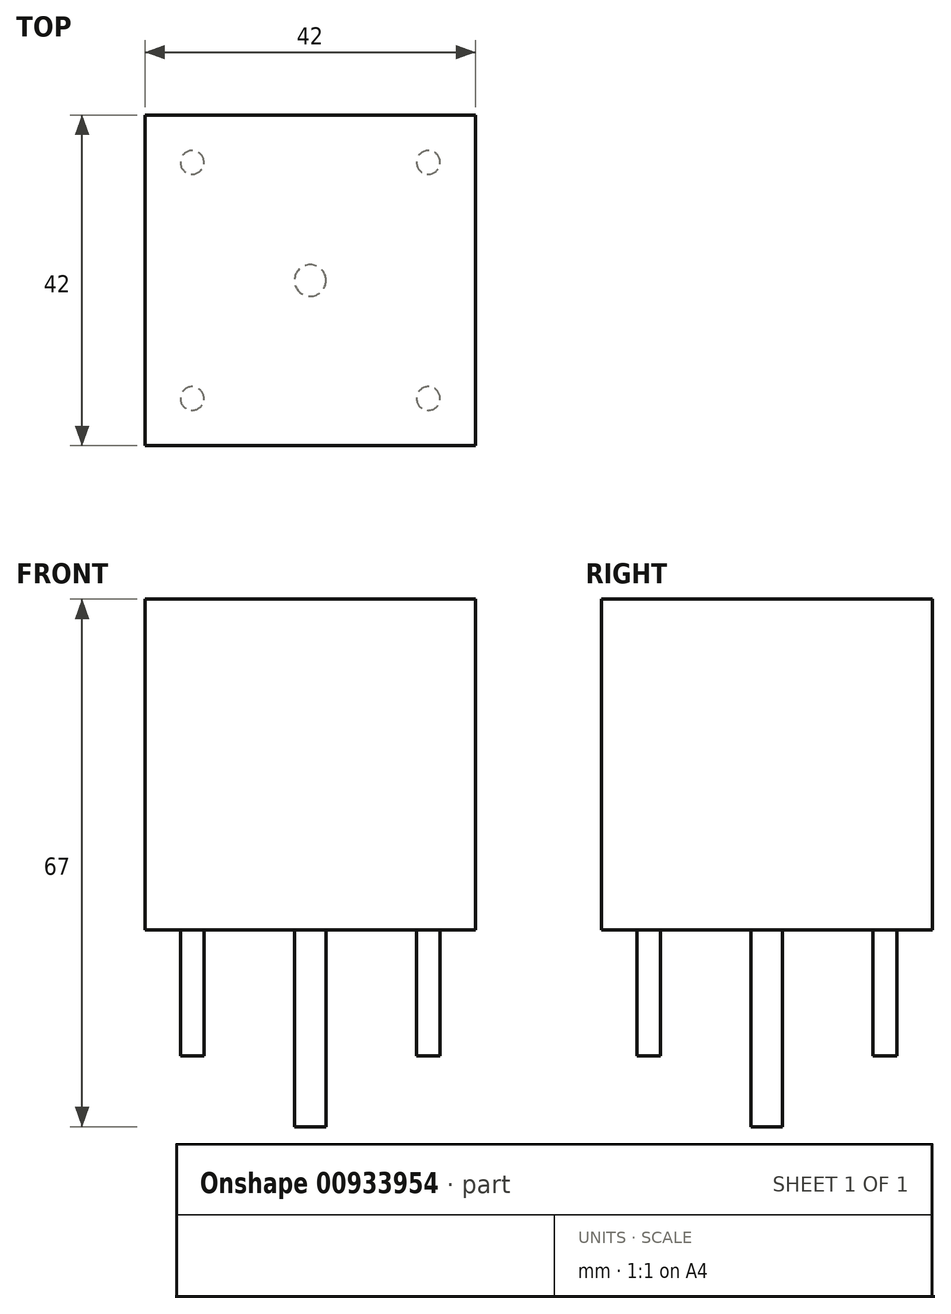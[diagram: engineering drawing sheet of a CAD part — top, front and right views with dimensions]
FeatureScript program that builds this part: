
annotation { "Feature Type Name" : "Feature", "Feature Type Description" : "" }
export const myFeature = defineFeature(function(context is Context, id is Id, definition is map)
    precondition{}
    {
        {
            var Q0;
            Q0=qCreatedBy(makeId("Top.planeOp"),FACE);
            var sketch = newSketch(context, id + "F0", { "sketchPlane" : qUnion([Q0])});
            skLineSegment(sketch, "E0.bottom", {"start": v(21, -21) * mm, "end": v(-21, -21) * mm});
            skLineSegment(sketch, "E0.top", {"start": v(21, 21) * mm, "end": v(-21, 21) * mm});
            skLineSegment(sketch, "E0.left", {"start": v(21, -21) * mm, "end": v(21, 21) * mm});
            skLineSegment(sketch, "E0.right", {"start": v(-21, -21) * mm, "end": v(-21, 21) * mm});
            skPoint(sketch, "E0.middle", {"position": v(0, 0) * mm});
            skSolve(sketch);
        }
        {
            var Q0;
            Q0=makeQuery(id+"F0.imprint","IMPRINT",FACE,{"disambiguationData":[TD([[makeQuery(id+"F0.imprint","IMPRINT",EDGE,{"derivedFrom":sQuery(id+"F0.wireOp",EDGE,"E0.bottom")}),-1.0]])]});
            extrude(context, id + "F1", {"entities" : qUnion([Q0]), "depth" : 42 * mm, "offsetDistance" : 25 * mm});
        }
        {
            var Q0;
            Q0=makeQuery(id+"F1.opExtrude","CAP_FACE",FACE,{"disambiguationData":[OSD([sQuery(id+"F0.wireOp",EDGE,"E0.bottom"),sQuery(id+"F0.wireOp",EDGE,"E0.top"),sQuery(id+"F0.wireOp",EDGE,"E0.left"),sQuery(id+"F0.wireOp",EDGE,"E0.right")])],"isStart":true});
            var sketch = newSketch(context, id + "F2", { "sketchPlane" : qUnion([Q0])});
            skCircle(sketch, "E1", {"center": v(0, 0) * mm, "radius": 2 * mm});
            skSolve(sketch);
        }
        {
            var Q0;
            Q0=makeQuery(id+"F2.imprint","IMPRINT",FACE,{"disambiguationData":[TD([[makeQuery(id+"F2.imprint","IMPRINT",EDGE,{"derivedFrom":sQuery(id+"F2.wireOp",EDGE,"E1")}),1.0]])]});
            extrude(context, id + "F3", {"entities" : qUnion([Q0]), "operationType" : NewBodyOperationType.ADD, "depth" : 25 * mm, "offsetDistance" : 25 * mm});
        }
        {
            var Q0;
            Q0=makeQuery(id+"F1.opExtrude","CAP_FACE",FACE,{"disambiguationData":[OSD([sQuery(id+"F0.wireOp",EDGE,"E0.bottom"),sQuery(id+"F0.wireOp",EDGE,"E0.top"),sQuery(id+"F0.wireOp",EDGE,"E0.left"),sQuery(id+"F0.wireOp",EDGE,"E0.right")])],"isStart":true});
            var sketch = newSketch(context, id + "F4", { "sketchPlane" : qUnion([Q0])});
            skLineSegment(sketch, "E2.bottom", {"start": v(15, 15) * mm, "end": v(-15, 15) * mm, "construction": true});
            skLineSegment(sketch, "E2.top", {"start": v(15, -15) * mm, "end": v(-15, -15) * mm, "construction": true});
            skLineSegment(sketch, "E2.left", {"start": v(15, 15) * mm, "end": v(15, -15) * mm, "construction": true});
            skLineSegment(sketch, "E2.right", {"start": v(-15, 15) * mm, "end": v(-15, -15) * mm, "construction": true});
            skPoint(sketch, "E2.middle", {"position": v(0, 0) * mm});
            skCircle(sketch, "E3", {"center": v(-15, 15) * mm, "radius": 1.5 * mm});
            skCircle(sketch, "E4", {"center": v(15, 15) * mm, "radius": 1.5 * mm});
            skCircle(sketch, "E5", {"center": v(15, -15) * mm, "radius": 1.5 * mm});
            skCircle(sketch, "E6", {"center": v(-15, -15) * mm, "radius": 1.5 * mm});
            skSolve(sketch);
        }
        {
            var Q0;
            Q0=makeQuery(id+"F4.imprint","IMPRINT",FACE,{"disambiguationData":[TD([[makeQuery(id+"F4.imprint","IMPRINT",EDGE,{"derivedFrom":sQuery(id+"F4.wireOp",EDGE,"E3")}),1.0]])]});
            var Q1;
            Q1=makeQuery(id+"F4.imprint","IMPRINT",FACE,{"disambiguationData":[TD([[makeQuery(id+"F4.imprint","IMPRINT",EDGE,{"derivedFrom":sQuery(id+"F4.wireOp",EDGE,"E4")}),1.0]])]});
            var Q2;
            Q2=makeQuery(id+"F4.imprint","IMPRINT",FACE,{"disambiguationData":[TD([[makeQuery(id+"F4.imprint","IMPRINT",EDGE,{"derivedFrom":sQuery(id+"F4.wireOp",EDGE,"E5")}),1.0]])]});
            var Q3;
            Q3=makeQuery(id+"F4.imprint","IMPRINT",FACE,{"disambiguationData":[TD([[makeQuery(id+"F4.imprint","IMPRINT",EDGE,{"derivedFrom":sQuery(id+"F4.wireOp",EDGE,"E6")}),1.0]])]});
            extrude(context, id + "F5", {"entities" : qUnion([Q0, Q1, Q2, Q3]), "operationType" : NewBodyOperationType.ADD, "depth" : 16 * mm, "offsetDistance" : 25 * mm});
        }
    });
